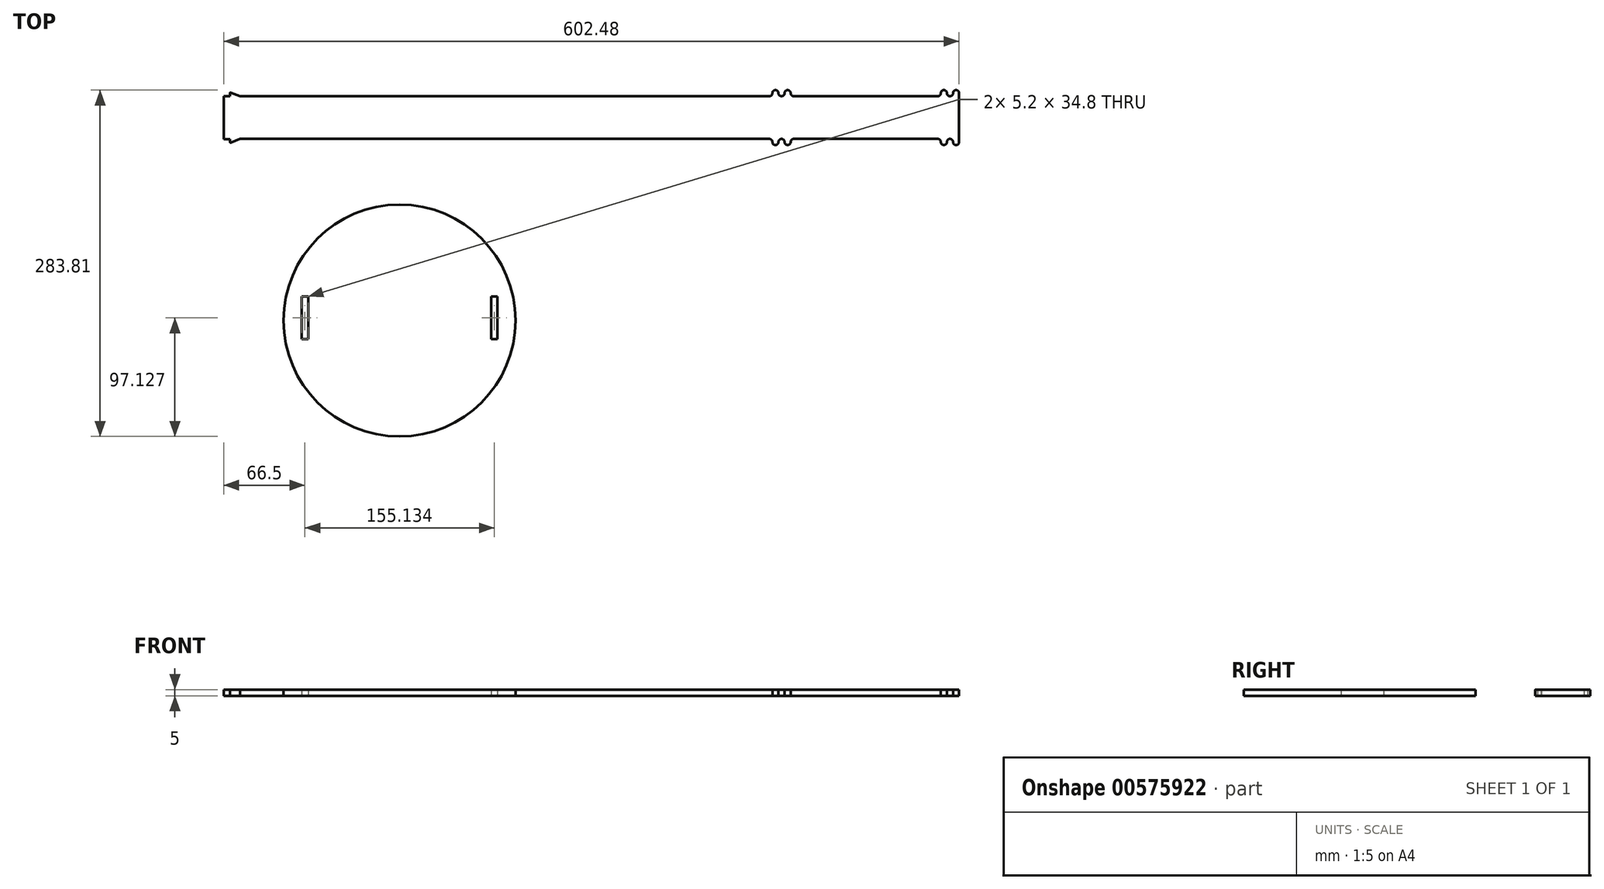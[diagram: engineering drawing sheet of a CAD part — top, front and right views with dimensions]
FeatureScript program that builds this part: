
annotation { "Feature Type Name" : "Feature", "Feature Type Description" : "" }
export const myFeature = defineFeature(function(context is Context, id is Id, definition is map)
    precondition{}
    {
        {
            var Q0;
            Q0=qCreatedBy(makeId("Top.planeOp"),FACE);
            var sketch = newSketch(context, id + "F0", { "sketchPlane" : qUnion([Q0])});
            skLineSegment(sketch, "E0", {"start": v(314, 42.66) * mm, "end": v(314, 45.16) * mm});
            skLineSegment(sketch, "E1", {"start": v(311.5, 47.66) * mm, "end": v(311.5, 47.66) * mm});
            skLineSegment(sketch, "E2", {"start": v(309, 45.16) * mm, "end": v(309, 45.16) * mm});
            skLineSegment(sketch, "E3", {"start": v(304, 47.66) * mm, "end": v(304, 47.66) * mm});
            skLineSegment(sketch, "E4", {"start": v(301.5, 47.66) * mm, "end": v(301.5, 47.66) * mm});
            skLineSegment(sketch, "E5", {"start": v(299, 45.16) * mm, "end": v(299, 45.16) * mm});
            skPoint(sketch, "E6.newPointB", {"position": v(-286, 42.66) * mm});
            skLineSegment(sketch, "E7", {"start": v(168.5, 42.66) * mm, "end": v(168.5, 42.66) * mm});
            skPoint(sketch, "E8.visualSharp", {"position": v(304, 42.66) * mm});
            skArc(sketch, "E8.filletArc", {"start": v(304, 45.16) * mm, "mid": v(304.74, 43.4) * mm, "end": v(306.5, 42.66) * mm});
            skPoint(sketch, "E9.visualSharp", {"position": v(309, 42.66) * mm});
            skArc(sketch, "E9.filletArc", {"start": v(306.5, 42.66) * mm, "mid": v(308.28, 43.4) * mm, "end": v(309, 45.16) * mm});
            skPoint(sketch, "E10.visualSharp", {"position": v(304, 47.66) * mm});
            skArc(sketch, "E10.filletArc", {"start": v(304, 45.16) * mm, "mid": v(303.28, 46.93) * mm, "end": v(301.5, 47.66) * mm});
            skPoint(sketch, "E11.visualSharp", {"position": v(309, 47.66) * mm});
            skArc(sketch, "E11.filletArc", {"start": v(311.5, 47.66) * mm, "mid": v(309.74, 46.93) * mm, "end": v(309, 45.16) * mm});
            skPoint(sketch, "E12.visualSharp", {"position": v(314, 47.66) * mm});
            skArc(sketch, "E12.filletArc", {"start": v(314, 45.16) * mm, "mid": v(313.28, 46.93) * mm, "end": v(311.5, 47.66) * mm});
            skPoint(sketch, "E13.visualSharp", {"position": v(299, 47.66) * mm});
            skArc(sketch, "E13.filletArc", {"start": v(301.5, 47.66) * mm, "mid": v(299.74, 46.93) * mm, "end": v(299, 45.16) * mm});
            skLineSegment(sketch, "E14", {"start": v(176, 45.16) * mm, "end": v(176, 45.16) * mm});
            skLineSegment(sketch, "E15", {"start": v(173.5, 47.66) * mm, "end": v(173.5, 47.66) * mm});
            skLineSegment(sketch, "E16", {"start": v(163.5, 47.66) * mm, "end": v(163.5, 47.66) * mm});
            skLineSegment(sketch, "E17", {"start": v(161, 45.16) * mm, "end": v(161, 45.16) * mm});
            skLineSegment(sketch, "E18", {"start": v(166, 45.16) * mm, "end": v(166, 45.16) * mm});
            skLineSegment(sketch, "E19", {"start": v(171, 45.16) * mm, "end": v(171, 45.16) * mm});
            skLineSegment(sketch, "E20", {"start": v(128.28, 58.67) * mm, "end": v(128.28, 57.84) * mm});
            skLineSegment(sketch, "E21", {"start": v(130.78, 55.34) * mm, "end": v(131.51, 55.34) * mm});
            skPoint(sketch, "E22.visualSharp", {"position": v(128.28, 55.34) * mm});
            skArc(sketch, "E22.filletArc", {"start": v(128.28, 57.84) * mm, "mid": v(129.01, 56.08) * mm, "end": v(130.78, 55.34) * mm});
            skLineSegment(sketch, "E23", {"start": v(145.17, 53.94) * mm, "end": v(145.17, 51.36) * mm});
            skLineSegment(sketch, "E24", {"start": v(147.67, 48.86) * mm, "end": v(152, 48.86) * mm});
            skPoint(sketch, "E25.visualSharp", {"position": v(145.17, 48.86) * mm});
            skArc(sketch, "E25.filletArc", {"start": v(145.17, 51.36) * mm, "mid": v(145.9, 49.6) * mm, "end": v(147.67, 48.86) * mm});
            skArc(sketch, "E26.filletArc", {"start": v(166, 45.16) * mm, "mid": v(166.73, 43.4) * mm, "end": v(168.5, 42.66) * mm});
            skArc(sketch, "E27.filletArc", {"start": v(168.5, 42.66) * mm, "mid": v(170.27, 43.4) * mm, "end": v(171, 45.16) * mm});
            skPoint(sketch, "E28.visualSharp", {"position": v(176, 47.66) * mm});
            skArc(sketch, "E28.filletArc", {"start": v(176, 45.16) * mm, "mid": v(175.27, 46.93) * mm, "end": v(173.5, 47.66) * mm});
            skPoint(sketch, "E29.visualSharp", {"position": v(171, 47.66) * mm});
            skArc(sketch, "E29.filletArc", {"start": v(173.5, 47.66) * mm, "mid": v(171.73, 46.93) * mm, "end": v(171, 45.16) * mm});
            skPoint(sketch, "E30.visualSharp", {"position": v(166, 47.66) * mm});
            skArc(sketch, "E30.filletArc", {"start": v(166, 45.16) * mm, "mid": v(165.27, 46.93) * mm, "end": v(163.5, 47.66) * mm});
            skPoint(sketch, "E31.visualSharp", {"position": v(161, 47.66) * mm});
            skArc(sketch, "E31.filletArc", {"start": v(163.5, 47.66) * mm, "mid": v(161.73, 46.93) * mm, "end": v(161, 45.16) * mm});
            skLineSegment(sketch, "E32", {"start": v(178.5, 42.66) * mm, "end": v(296.5, 42.66) * mm});
            skPoint(sketch, "E33.visualSharp", {"position": v(299, 42.66) * mm});
            skArc(sketch, "E33.filletArc", {"start": v(296.5, 42.66) * mm, "mid": v(298.28, 43.4) * mm, "end": v(299, 45.16) * mm});
            skPoint(sketch, "E34.visualSharp", {"position": v(176, 42.66) * mm});
            skArc(sketch, "E34.filletArc", {"start": v(176, 45.16) * mm, "mid": v(176.73, 43.4) * mm, "end": v(178.5, 42.66) * mm});
            skPoint(sketch, "E35.visualSharp", {"position": v(161, 42.66) * mm});
            skArc(sketch, "E35.filletArc", {"start": v(158.5, 42.66) * mm, "mid": v(160.27, 43.4) * mm, "end": v(161, 45.16) * mm});
            skArc(sketch, "E36", {"start": v(-219.37, -138.92) * mm, "mid": v(-219.4, -141.15) * mm, "end": v(-219.37, -143.38) * mm});
            skLineSegment(sketch, "E37", {"start": v(314, 42.66) * mm, "end": v(314, 25.16) * mm});
            skPoint(sketch, "E38.orphan", {"position": v(-288.47, 7.66) * mm});
            skLineSegment(sketch, "E39.MirrorCS", {"start": v(314, 7.66) * mm, "end": v(314, 25.16) * mm});
            skLineSegment(sketch, "E40.MirrorCS", {"start": v(314, 7.66) * mm, "end": v(314, 5.16) * mm});
            skArc(sketch, "E41.MirrorCS", {"start": v(314, 5.16) * mm, "mid": v(313.28, 3.4) * mm, "end": v(311.5, 2.66) * mm});
            skArc(sketch, "E42.MirrorCS", {"start": v(311.5, 2.66) * mm, "mid": v(309.74, 3.4) * mm, "end": v(309, 5.16) * mm});
            skArc(sketch, "E43.MirrorCS", {"start": v(306.5, 7.66) * mm, "mid": v(308.28, 6.93) * mm, "end": v(309, 5.16) * mm});
            skArc(sketch, "E44.MirrorCS", {"start": v(304, 5.16) * mm, "mid": v(304.74, 6.93) * mm, "end": v(306.5, 7.66) * mm});
            skArc(sketch, "E45.MirrorCS", {"start": v(304, 5.16) * mm, "mid": v(303.28, 3.4) * mm, "end": v(301.5, 2.66) * mm});
            skArc(sketch, "E46.MirrorCS", {"start": v(301.5, 2.66) * mm, "mid": v(299.74, 3.4) * mm, "end": v(299, 5.16) * mm});
            skArc(sketch, "E47.MirrorCS", {"start": v(296.5, 7.66) * mm, "mid": v(298.28, 6.93) * mm, "end": v(299, 5.16) * mm});
            skLineSegment(sketch, "E48.MirrorCS", {"start": v(178.5, 7.66) * mm, "end": v(296.5, 7.66) * mm});
            skArc(sketch, "E49.MirrorCS", {"start": v(176, 5.16) * mm, "mid": v(176.73, 6.93) * mm, "end": v(178.5, 7.66) * mm});
            skArc(sketch, "E50.MirrorCS", {"start": v(176, 5.16) * mm, "mid": v(175.27, 3.4) * mm, "end": v(173.5, 2.66) * mm});
            skArc(sketch, "E51.MirrorCS", {"start": v(173.5, 2.66) * mm, "mid": v(171.73, 3.4) * mm, "end": v(171, 5.16) * mm});
            skArc(sketch, "E52.MirrorCS", {"start": v(168.5, 7.66) * mm, "mid": v(170.27, 6.93) * mm, "end": v(171, 5.16) * mm});
            skArc(sketch, "E53.MirrorCS", {"start": v(166, 5.16) * mm, "mid": v(166.73, 6.93) * mm, "end": v(168.5, 7.66) * mm});
            skArc(sketch, "E54.MirrorCS", {"start": v(166, 5.16) * mm, "mid": v(165.27, 3.4) * mm, "end": v(163.5, 2.66) * mm});
            skArc(sketch, "E55.MirrorCS", {"start": v(163.5, 2.66) * mm, "mid": v(161.73, 3.4) * mm, "end": v(161, 5.16) * mm});
            skArc(sketch, "E56.MirrorCS", {"start": v(158.5, 7.66) * mm, "mid": v(160.27, 6.93) * mm, "end": v(161, 5.16) * mm});
            skLineSegment(sketch, "E57", {"start": v(-219.37, -121.62) * mm, "end": v(-219.37, -156.42) * mm});
            skLineSegment(sketch, "E58", {"start": v(-219.37, -156.42) * mm, "end": v(-224.57, -156.42) * mm});
            skLineSegment(sketch, "E59.MirrorCS", {"start": v(-64.24, -156.42) * mm, "end": v(-64.24, -121.62) * mm});
            skLineSegment(sketch, "E60.MirrorCS", {"start": v(-69.44, -138.92) * mm, "end": v(-69.44, -121.62) * mm});
            skLineSegment(sketch, "E61.MirrorCS", {"start": v(-69.44, -121.62) * mm, "end": v(-69.44, -156.42) * mm});
            skLineSegment(sketch, "E62.MirrorCS", {"start": v(-69.44, -156.42) * mm, "end": v(-64.24, -156.42) * mm});
            skCircle(sketch, "E63", {"center": v(-144.4, -141.15) * mm, "radius": 95 * mm});
            skArc(sketch, "E64.trimOffspring", {"start": v(-69.44, -143.38) * mm, "mid": v(-69.4, -141.15) * mm, "end": v(-69.44, -138.92) * mm});
            skLineSegment(sketch, "E65", {"start": v(-219.37, -121.62) * mm, "end": v(-224.57, -121.62) * mm});
            skPoint(sketch, "E66.orphan", {"position": v(-224.67, -121.42) * mm});
            skPoint(sketch, "E67.start.orphan", {"position": v(-219.37, -121.42) * mm});
            skLineSegment(sketch, "E68", {"start": v(-224.57, -121.62) * mm, "end": v(-224.57, -156.42) * mm});
            skLineSegment(sketch, "E69", {"start": v(-69.44, -121.62) * mm, "end": v(-64.24, -121.62) * mm});
            skPoint(sketch, "E70.MirrorCS.start.orphan", {"position": v(-64.24, -121.42) * mm});
            skLineSegment(sketch, "E71.trimOffspring", {"start": v(-275.09, 7.66) * mm, "end": v(158.5, 7.66) * mm});
            skLineSegment(sketch, "E72", {"start": v(-283.47, 7.46) * mm, "end": v(-288.47, 7.46) * mm});
            skLineSegment(sketch, "E73", {"start": v(-283.47, 42.86) * mm, "end": v(-283.47, 45.14) * mm});
            skLineSegment(sketch, "E74", {"start": v(-282.8, 45.6) * mm, "end": v(-275.09, 42.66) * mm});
            skLineSegment(sketch, "E75", {"start": v(-283.47, 7.46) * mm, "end": v(-283.47, 5.2) * mm});
            skLineSegment(sketch, "E76", {"start": v(-282.8, 4.72) * mm, "end": v(-275.09, 7.66) * mm});
            skLineSegment(sketch, "E77", {"start": v(-275.09, 42.66) * mm, "end": v(158.5, 42.66) * mm});
            skPoint(sketch, "E78.visualSharp", {"position": v(-283.47, 4.46) * mm});
            skPoint(sketch, "E79.visualSharp", {"position": v(-283.47, 45.86) * mm});
            skArc(sketch, "E79.filletArc", {"start": v(-282.8, 45.6) * mm, "mid": v(-283.25, 45.55) * mm, "end": v(-283.47, 45.14) * mm});
            skPoint(sketch, "E80.visualSharp", {"position": v(-283.47, 4.55) * mm});
            skLineSegment(sketch, "E80.filletArc", {"start": v(-283.47, 4.55) * mm, "end": v(-283.47, 4.55) * mm});
            skArc(sketch, "E81.filletArc", {"start": v(-283.47, 5.2) * mm, "mid": v(-283.25, 4.78) * mm, "end": v(-282.8, 4.72) * mm});
            skPoint(sketch, "E82.left.end.orphan", {"position": v(-288.47, 25.16) * mm});
            skPoint(sketch, "E83.end.orphan", {"position": v(-288.47, 42.66) * mm});
            skLineSegment(sketch, "E84", {"start": v(-288.47, 7.46) * mm, "end": v(-288.47, 42.66) * mm});
            skLineSegment(sketch, "E85", {"start": v(-288.47, 42.66) * mm, "end": v(-283.47, 42.66) * mm});
            skLineSegment(sketch, "E86", {"start": v(-283.47, 42.66) * mm, "end": v(-283.47, 42.86) * mm});
            skPoint(sketch, "E87.end.orphan", {"position": v(-288.47, 42.86) * mm});
            skSolve(sketch);
        }
        {
            var Q0;
            {var subQ11=sQuery(id+"F0.wireOp",EDGE,"E58");Q0=makeQuery(id+"F0.imprint","IMPRINT",FACE,{"disambiguationData":[TD([[makeQuery(id+"F0.imprint","IMPRINT",EDGE,{"derivedFrom":subQ11}),1.0]])]});}
            var Q1;
            Q1=makeQuery(id+"F0.imprint","IMPRINT",FACE,{"disambiguationData":[TD([[makeQuery(id+"F0.imprint","IMPRINT",EDGE,{"derivedFrom":sQuery(id+"F0.wireOp",EDGE,"E0")}),1.0]])]});
            extrude(context, id + "F1", {"entities" : qUnion([Q0, Q1]), "depth" : 5 * mm, "offsetDistance" : 25 * mm});
        }
    });
